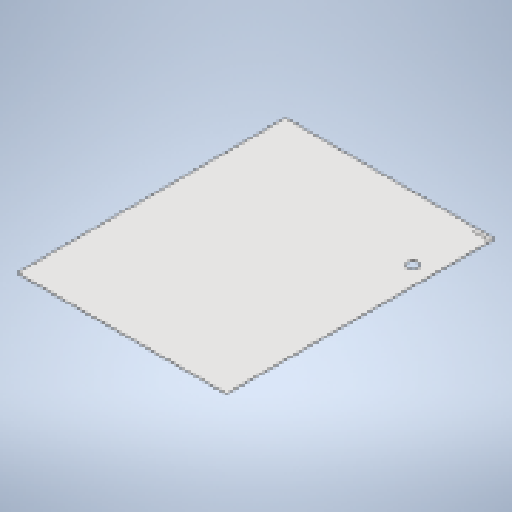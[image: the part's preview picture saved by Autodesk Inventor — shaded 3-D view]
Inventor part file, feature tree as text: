
AUTODESK INVENTOR PART (.ipt)
format: ipt  version: 2025 (Build 290162010, 162A)  size: 232,960 bytes
history: native  units: mm
features: other x3, sketch x3, sheet_metal_op x1, extrude x1
ambient origin geometry x8: Origin, YZ Plane, XZ Plane, XY Plane, X Axis, Y Axis, Z Axis, Center Point
bodies: Body1 (feature_tree)
feature tree (8):
  sheet_metal_op  "Face3"
  other  "Mark1"
  extrude  "Extrusion3"  Depth=1895.0mm
  sketch  "Sketch6"  dims[d40=1479.0mm d41=1895.0mm]
  other  "Plate5"
  sketch  "Sketch7"  dims[d42=3.0mm]
  sketch  "Sketch8"  dims[d43=200.0mm d44=15.0mm d45=25.0mm d46=25.0mm d47=80.0mm d48=1350.0mm d49=450.0mm d50=10.0mm d51=0.0mm]
  other  "Definition1"
